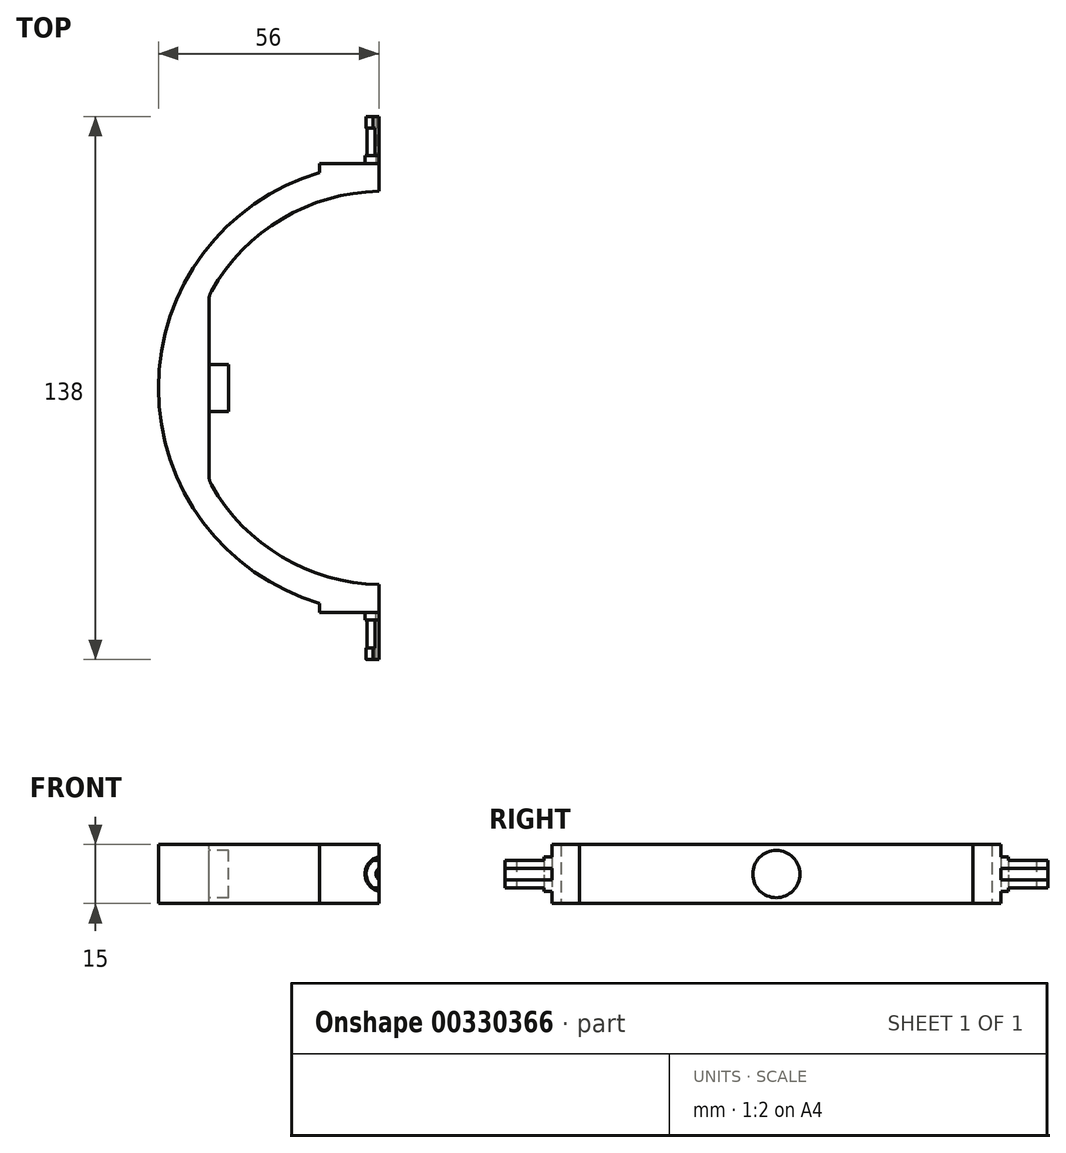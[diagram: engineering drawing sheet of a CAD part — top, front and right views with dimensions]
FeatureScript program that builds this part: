
annotation { "Feature Type Name" : "Feature", "Feature Type Description" : "" }
export const myFeature = defineFeature(function(context is Context, id is Id, definition is map)
    precondition{}
    {
        {
            var Q0;
            Q0=qCreatedBy(makeId("Top.planeOp"),FACE);
            var sketch = newSketch(context, id + "F0", { "sketchPlane" : qUnion([Q0])});
            skArc(sketch, "E0", {"start": v(0, 50) * mm, "mid": v(-25.76, 42.85) * mm, "end": v(-44.16, 23.45) * mm});
            skLineSegment(sketch, "E1", {"start": v(-44.16, 23.45) * mm, "end": v(-44.16, -23.45) * mm});
            skArc(sketch, "E2", {"start": v(-16, 54.7) * mm, "mid": v(-57, 0) * mm, "end": v(-16, -54.7) * mm});
            skLineSegment(sketch, "E3", {"start": v(0, 57) * mm, "end": v(0, 50) * mm});
            skLineSegment(sketch, "E4", {"start": v(0, -50) * mm, "end": v(0, -57) * mm});
            skArc(sketch, "E5.trimOffspring", {"start": v(-44.16, -23.45) * mm, "mid": v(-25.76, -42.85) * mm, "end": v(0, -50) * mm});
            skLineSegment(sketch, "E6", {"start": v(0, -57) * mm, "end": v(-16, -57) * mm});
            skLineSegment(sketch, "E7", {"start": v(-16, -57) * mm, "end": v(-16, -54.7) * mm});
            skLineSegment(sketch, "E8", {"start": v(0, 57) * mm, "end": v(-16, 57) * mm});
            skLineSegment(sketch, "E9", {"start": v(-16, 57) * mm, "end": v(-16, 54.7) * mm});
            skSolve(sketch);
        }
        {
            var Q0;
            Q0=makeQuery(id+"F0.imprint","IMPRINT",FACE,{"disambiguationData":[TD([[makeQuery(id+"F0.imprint","IMPRINT",EDGE,{"derivedFrom":sQuery(id+"F0.wireOp",EDGE,"E0")}),-1.0]])]});
            extrude(context, id + "F1", {"entities" : qUnion([Q0]), "depth" : 15 * mm});
        }
        {
            var Q0;
            Q0=makeQuery(id+"F1.opExtrude","SWEPT_FACE",FACE,{"disambiguationData":[OSD([sQuery(id+"F0.wireOp",EDGE,"E1")])]});
            var sketch = newSketch(context, id + "F2", { "sketchPlane" : qUnion([Q0])});
            skLineSegment(sketch, "E10", {"start": v(-23.45, 15) * mm, "end": v(23.45, 0) * mm, "construction": true});
            skLineSegment(sketch, "E11", {"start": v(-23.45, 0) * mm, "end": v(23.45, 15) * mm, "construction": true});
            skCircle(sketch, "E12", {"center": v(0, 7.5) * mm, "radius": 6 * mm});
            skSolve(sketch);
        }
        {
            var Q0;
            Q0=makeQuery(id+"F2.imprint","IMPRINT",FACE,{"disambiguationData":[TD([[makeQuery(id+"F2.imprint","IMPRINT",EDGE,{"derivedFrom":sQuery(id+"F2.wireOp",EDGE,"E12")}),1.0]])]});
            extrude(context, id + "F3", {"entities" : qUnion([Q0]), "operationType" : NewBodyOperationType.ADD, "depth" : 5 * mm});
        }
        {
            var Q0;
            Q0=makeQuery(id+"F1.opExtrude","SWEPT_EDGE",EDGE,{"disambiguationData":[OSD([sQuery(id+"F0.wireOp",EDGE,"E0"),sQuery(id+"F0.wireOp",EDGE,"E1")])]});
            var Q1;
            Q1=makeQuery(id+"F1.opExtrude","SWEPT_EDGE",EDGE,{"disambiguationData":[OSD([sQuery(id+"F0.wireOp",EDGE,"E1"),sQuery(id+"F0.wireOp",EDGE,"E5.trimOffspring")])]});
            fillet(context, id + "F4", {"entities" : qUnion([Q0, Q1]), "radius" : 5 * mm, "tangentPropagation" : true, "allowEdgeOverflow" : false});
        }
        {
            var Q0;
            Q0=makeQuery(id+"F1.opExtrude","SWEPT_FACE",FACE,{"disambiguationData":[OSD([sQuery(id+"F0.wireOp",EDGE,"E6")])]});
            var sketch = newSketch(context, id + "F5", { "sketchPlane" : qUnion([Q0])});
            skArc(sketch, "E13", {"start": v(0, 12) * mm, "mid": v(-4.5, 7.5) * mm, "end": v(0, 3) * mm});
            skArc(sketch, "E14", {"start": v(0, 9.25) * mm, "mid": v(-1.75, 7.5) * mm, "end": v(0, 5.75) * mm});
            skLineSegment(sketch, "E15", {"start": v(0, 12) * mm, "end": v(0, 9.25) * mm});
            skLineSegment(sketch, "E16", {"start": v(0, 9.25) * mm, "end": v(0, 5.75) * mm});
            skLineSegment(sketch, "E17", {"start": v(0, 5.75) * mm, "end": v(0, 3) * mm});
            skLineSegment(sketch, "E18", {"start": v(0, 5.75) * mm, "end": v(0, 9.25) * mm});
            skSolve(sketch);
        }
        {
            var Q0;
            Q0=makeQuery(id+"F5.imprint","IMPRINT",FACE,{"disambiguationData":[TD([[makeQuery(id+"F5.imprint","IMPRINT",EDGE,{"derivedFrom":sQuery(id+"F5.wireOp",EDGE,"E13")}),1.0]])]});
            extrude(context, id + "F6", {"entities" : qUnion([Q0]), "operationType" : NewBodyOperationType.ADD, "depth" : 2 * mm});
        }
        {
            var Q0;
            Q0=makeQuery(id+"F6.opExtrude","CAP_FACE",FACE,{"disambiguationData":[OSD([sQuery(id+"F5.wireOp",EDGE,"E13"),sQuery(id+"F5.wireOp",EDGE,"E14"),sQuery(id+"F5.wireOp",EDGE,"E15"),sQuery(id+"F5.wireOp",EDGE,"E17")])],"isStart":false});
            var sketch = newSketch(context, id + "F7", { "sketchPlane" : qUnion([Q0])});
            skArc(sketch, "E19", {"start": v(0, 11.5) * mm, "mid": v(-4, 7.5) * mm, "end": v(0, 3.5) * mm});
            skLineSegment(sketch, "E20", {"start": v(0, 11.5) * mm, "end": v(0, 9.25) * mm});
            skLineSegment(sketch, "E21", {"start": v(0, 9.25) * mm, "end": v(0, 5.75) * mm});
            skLineSegment(sketch, "E22", {"start": v(0, 5.75) * mm, "end": v(0, 3.5) * mm});
            skSolve(sketch);
        }
        {
            var Q0;
            Q0=makeQuery(id+"F7.imprint","IMPRINT",FACE,{"disambiguationData":[TD([[makeQuery(id+"F7.imprint","IMPRINT",EDGE,{"derivedFrom":sQuery(id+"F7.wireOp",EDGE,"E19")}),1.0]])]});
            extrude(context, id + "F8", {"entities" : qUnion([Q0]), "operationType" : NewBodyOperationType.ADD, "depth" : 7 * mm, "offsetDistance" : 25 * mm});
        }
        {
            var Q0;
            Q0=makeQuery(id+"F8.opExtrude","CAP_FACE",FACE,{"disambiguationData":[OSD([sQuery(id+"F5.wireOp",EDGE,"E14"),sQuery(id+"F7.wireOp",EDGE,"E19"),sQuery(id+"F7.wireOp",EDGE,"E20"),sQuery(id+"F7.wireOp",EDGE,"E22")])],"isStart":false});
            var sketch = newSketch(context, id + "F9", { "sketchPlane" : qUnion([Q0])});
            skArc(sketch, "E23", {"start": v(0, 11.75) * mm, "mid": v(-4.25, 7.5) * mm, "end": v(0, 3.25) * mm});
            skLineSegment(sketch, "E24", {"start": v(0, 3.25) * mm, "end": v(0, 11.75) * mm});
            skSolve(sketch);
        }
        {
            var Q0;
            Q0 = qSketchRegion(id + "F9", true);
            extrude(context, id + "F10", {"entities" : qUnion([Q0]), "operationType" : NewBodyOperationType.ADD, "depth" : 3 * mm});
        }
        {
            var Q0;
            {var subQ0=sQuery(id+"F5.wireOp",EDGE,"E14");var subQ1=sQuery(id+"F9.wireOp",EDGE,"E24");Q0=makeQuery(id+"F10.boolean.opBoolean","SPLIT",FACE,{"disambiguationData":[TD([makeQuery(id+"F6.opExtrude","SWEPT_FACE",FACE,{"disambiguationData":[OSD([subQ0])]})])],"derivedFrom":makeQuery(id+"F10.opExtrude","CAP_FACE",FACE,{"disambiguationData":[OSD([sQuery(id+"F9.wireOp",EDGE,"E23"),subQ1])],"isStart":true})});}
            extrude(context, id + "F11", {"entities" : qUnion([Q0]), "operationType" : NewBodyOperationType.REMOVE, "oppositeDirection" : true, "depth" : 25 * mm});
        }
        {
            var Q0;
            Q0=makeQuery(id+"F1.opExtrude","SWEPT_BODY",BODY,{"disambiguationData":[OSD([sQuery(id+"F0.wireOp",EDGE,"E0"),sQuery(id+"F0.wireOp",EDGE,"E1"),sQuery(id+"F0.wireOp",EDGE,"E2"),sQuery(id+"F0.wireOp",EDGE,"E3"),sQuery(id+"F0.wireOp",EDGE,"E4"),sQuery(id+"F0.wireOp",EDGE,"E5.trimOffspring"),sQuery(id+"F0.wireOp",EDGE,"E6"),sQuery(id+"F0.wireOp",EDGE,"E7"),sQuery(id+"F0.wireOp",EDGE,"E8"),sQuery(id+"F0.wireOp",EDGE,"E9")])]});
            var Q1;
            Q1=qCreatedBy(makeId("Front.planeOp"),FACE);
            mirror(context, id + "F12", {"operationType" : NewBodyOperationType.ADD, "entities" : qUnion([Q0]), "mirrorPlane" : qUnion([Q1])});
        }
        {
            var Q0;
            Q0=qCreatedBy(makeId("Right.planeOp"),FACE);
            var sketch = newSketch(context, id + "F13", { "sketchPlane" : qUnion([Q0])});
            skLineSegment(sketch, "E25.bottom", {"start": v(-73.13, 21.61) * mm, "end": v(73.72, 21.61) * mm});
            skLineSegment(sketch, "E25.top", {"start": v(-73.13, -6.51) * mm, "end": v(73.72, -6.51) * mm});
            skLineSegment(sketch, "E25.left", {"start": v(-73.13, 21.61) * mm, "end": v(-73.13, -6.51) * mm});
            skLineSegment(sketch, "E25.right", {"start": v(73.72, 21.61) * mm, "end": v(73.72, -6.51) * mm});
            skSolve(sketch);
        }
        {
            var Q0;
            Q0=makeQuery(id+"F13.imprint","IMPRINT",FACE,{"disambiguationData":[TD([[makeQuery(id+"F13.imprint","IMPRINT",EDGE,{"derivedFrom":sQuery(id+"F13.wireOp",EDGE,"E25.bottom")}),-1.0]])]});
            extrude(context, id + "F14", {"entities" : qUnion([Q0]), "operationType" : NewBodyOperationType.REMOVE, "oppositeDirection" : true, "depth" : 1 * mm});
        }
        {
            var Q0;
            Q0=qCreatedBy(makeId("Top.planeOp"),FACE);
            var sketch = newSketch(context, id + "F15", { "sketchPlane" : qUnion([Q0])});
            skLineSegment(sketch, "E26.bottom", {"start": v(-7.64, -70.53) * mm, "end": v(3.73, -70.53) * mm});
            skLineSegment(sketch, "E26.top", {"start": v(-7.64, -59) * mm, "end": v(3.73, -59) * mm});
            skLineSegment(sketch, "E26.left", {"start": v(-7.64, -70.53) * mm, "end": v(-7.64, -59) * mm});
            skLineSegment(sketch, "E26.right", {"start": v(3.73, -70.53) * mm, "end": v(3.73, -59) * mm});
            skLineSegment(sketch, "E27.bottom", {"start": v(-8.8, 59) * mm, "end": v(4.55, 59) * mm});
            skLineSegment(sketch, "E27.top", {"start": v(-8.8, 72.01) * mm, "end": v(4.55, 72.01) * mm});
            skLineSegment(sketch, "E27.left", {"start": v(-8.8, 59) * mm, "end": v(-8.8, 72.01) * mm});
            skLineSegment(sketch, "E27.right", {"start": v(4.55, 59) * mm, "end": v(4.55, 72.01) * mm});
            skSolve(sketch);
        }
        {
            var Q0;
            Q0=makeQuery(id+"F15.imprint","IMPRINT",FACE,{"disambiguationData":[TD([[makeQuery(id+"F15.imprint","IMPRINT",EDGE,{"derivedFrom":sQuery(id+"F15.wireOp",EDGE,"E26.bottom")}),1.0]])]});
            var Q1;
            Q1=makeQuery(id+"F15.imprint","IMPRINT",FACE,{"disambiguationData":[TD([[makeQuery(id+"F15.imprint","IMPRINT",EDGE,{"derivedFrom":sQuery(id+"F15.wireOp",EDGE,"E27.bottom")}),1.0]])]});
            extrude(context, id + "F16", {"entities" : qUnion([Q0, Q1]), "operationType" : NewBodyOperationType.REMOVE, "depth" : 4 * mm});
        }
        {
            var Q0;
            Q0=makeQuery(id+"F1.opExtrude","CAP_FACE",FACE,{"disambiguationData":[OSD([sQuery(id+"F0.wireOp",EDGE,"E0"),sQuery(id+"F0.wireOp",EDGE,"E1"),sQuery(id+"F0.wireOp",EDGE,"E2"),sQuery(id+"F0.wireOp",EDGE,"E3"),sQuery(id+"F0.wireOp",EDGE,"E4"),sQuery(id+"F0.wireOp",EDGE,"E5.trimOffspring"),sQuery(id+"F0.wireOp",EDGE,"E6"),sQuery(id+"F0.wireOp",EDGE,"E7"),sQuery(id+"F0.wireOp",EDGE,"E8"),sQuery(id+"F0.wireOp",EDGE,"E9")])],"isStart":false});
            var sketch = newSketch(context, id + "F17", { "sketchPlane" : qUnion([Q0])});
            skLineSegment(sketch, "E28.bottom", {"start": v(-14.22, 71.73) * mm, "end": v(5.3, 71.73) * mm});
            skLineSegment(sketch, "E28.top", {"start": v(-14.22, 59) * mm, "end": v(5.3, 59) * mm});
            skLineSegment(sketch, "E28.left", {"start": v(-14.22, 71.73) * mm, "end": v(-14.22, 59) * mm});
            skLineSegment(sketch, "E28.right", {"start": v(5.3, 71.73) * mm, "end": v(5.3, 59) * mm});
            skLineSegment(sketch, "E29.bottom", {"start": v(-12.24, -59) * mm, "end": v(6.71, -59) * mm});
            skLineSegment(sketch, "E29.top", {"start": v(-12.24, -69.75) * mm, "end": v(6.71, -69.75) * mm});
            skLineSegment(sketch, "E29.left", {"start": v(-12.24, -59) * mm, "end": v(-12.24, -69.75) * mm});
            skLineSegment(sketch, "E29.right", {"start": v(6.71, -59) * mm, "end": v(6.71, -69.75) * mm});
            skSolve(sketch);
        }
        {
            var Q0;
            Q0=makeQuery(id+"F17.imprint","IMPRINT",FACE,{"disambiguationData":[TD([[makeQuery(id+"F17.imprint","IMPRINT",EDGE,{"derivedFrom":sQuery(id+"F17.wireOp",EDGE,"E28.bottom")}),-1.0]])]});
            var Q1;
            Q1=makeQuery(id+"F17.imprint","IMPRINT",FACE,{"disambiguationData":[TD([[makeQuery(id+"F17.imprint","IMPRINT",EDGE,{"derivedFrom":sQuery(id+"F17.wireOp",EDGE,"E29.bottom")}),-1.0]])]});
            extrude(context, id + "F18", {"entities" : qUnion([Q0, Q1]), "operationType" : NewBodyOperationType.REMOVE, "oppositeDirection" : true, "depth" : 4 * mm});
        }
    });
